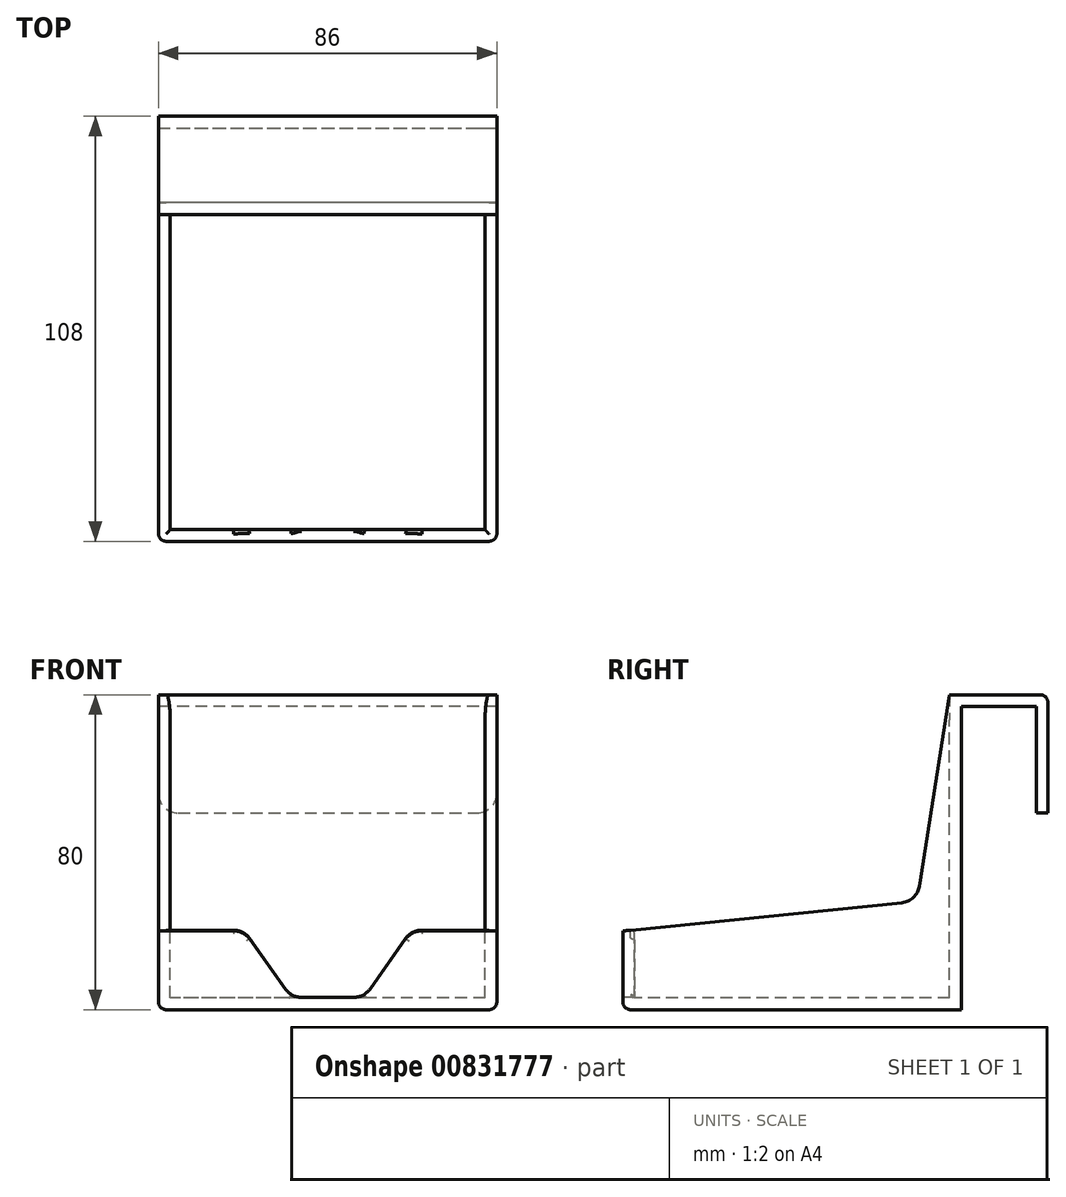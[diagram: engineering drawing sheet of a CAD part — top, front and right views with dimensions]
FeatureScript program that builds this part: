
annotation { "Feature Type Name" : "Feature", "Feature Type Description" : "" }
export const myFeature = defineFeature(function(context is Context, id is Id, definition is map)
    precondition{}
    {
        {
            var Q0;
            Q0=qCreatedBy(makeId("Top.planeOp"),FACE);
            var sketch = newSketch(context, id + "F0", { "sketchPlane" : qUnion([Q0])});
            skLineSegment(sketch, "E0.bottom", {"start": v(43, 43) * mm, "end": v(-43, 43) * mm});
            skLineSegment(sketch, "E0.top", {"start": v(43, -43) * mm, "end": v(-43, -43) * mm});
            skLineSegment(sketch, "E0.left", {"start": v(43, 43) * mm, "end": v(43, -43) * mm});
            skLineSegment(sketch, "E0.right", {"start": v(-43, 43) * mm, "end": v(-43, -43) * mm});
            skPoint(sketch, "E0.middle", {"position": v(0, 0) * mm});
            skLineSegment(sketch, "E1", {"start": v(-43, 43) * mm, "end": v(-43, 62) * mm});
            skLineSegment(sketch, "E2", {"start": v(43, 43) * mm, "end": v(43, 62) * mm});
            skLineSegment(sketch, "E3", {"start": v(-43, 62) * mm, "end": v(43, 62) * mm});
            skLineSegment(sketch, "E4", {"start": v(-43, 62) * mm, "end": v(-43, 64) * mm});
            skLineSegment(sketch, "E5", {"start": v(43, 62) * mm, "end": v(43, 64) * mm});
            skLineSegment(sketch, "E6", {"start": v(43, 64) * mm, "end": v(-43, 64) * mm});
            skSolve(sketch);
        }
        {
            var Q0;
            Q0=makeQuery(id+"F0.imprint","IMPRINT",FACE,{"disambiguationData":[TD([[makeQuery(id+"F0.imprint","IMPRINT",EDGE,{"derivedFrom":sQuery(id+"F0.wireOp",EDGE,"E0.bottom")}),1.0]])]});
            extrude(context, id + "F1", {"entities" : qUnion([Q0]), "depth" : 80 * mm, "offsetDistance" : 25 * mm});
        }
        {
            var Q0;
            Q0=makeQuery(id+"F1.opExtrude","CAP_FACE",FACE,{"disambiguationData":[OSD([sQuery(id+"F0.wireOp",EDGE,"E0.bottom"),sQuery(id+"F0.wireOp",EDGE,"E0.top"),sQuery(id+"F0.wireOp",EDGE,"E0.left"),sQuery(id+"F0.wireOp",EDGE,"E0.right")])],"isStart":false});
            var sketch = newSketch(context, id + "F2", { "sketchPlane" : qUnion([Q0])});
            skLineSegment(sketch, "E7", {"start": v(43, 43) * mm, "end": v(43, 62) * mm});
            skLineSegment(sketch, "E8", {"start": v(-43, 43) * mm, "end": v(-43, 62) * mm});
            skLineSegment(sketch, "E9", {"start": v(-43, 62) * mm, "end": v(43, 62) * mm});
            skLineSegment(sketch, "E10", {"start": v(-43, 62) * mm, "end": v(-43, 65) * mm});
            skLineSegment(sketch, "E11", {"start": v(43, 62) * mm, "end": v(43, 65) * mm});
            skLineSegment(sketch, "E12", {"start": v(-43, 65) * mm, "end": v(43, 65) * mm});
            skSolve(sketch);
        }
        {
            var Q0;
            Q0=makeQuery(id+"F2.imprint","IMPRINT",FACE,{"disambiguationData":[TD([[makeQuery(id+"F2.imprint","IMPRINT",EDGE,{"derivedFrom":sQuery(id+"F2.wireOp",EDGE,"E7")}),1.0]])]});
            extrude(context, id + "F3", {"entities" : qUnion([Q0]), "operationType" : NewBodyOperationType.ADD, "depth" : -3 * mm, "offsetDistance" : 25 * mm});
        }
        {
            var Q0;
            Q0=qSketchRegion(id+"F2",true);
            var Q1;
            Q1=makeQuery(id+"F2.imprint","IMPRINT",FACE,{"disambiguationData":[TD([[makeQuery(id+"F2.imprint","IMPRINT",EDGE,{"derivedFrom":sQuery(id+"F2.wireOp",EDGE,"E9")}),1.0]])]});
            extrude(context, id + "F4", {"entities" : qUnion([Q0, Q1]), "operationType" : NewBodyOperationType.ADD, "depth" : -30 * mm, "offsetDistance" : 25 * mm});
        }
        {
            var Q0;
            Q0=makeQuery(id+"F2.imprint","IMPRINT",FACE,{"disambiguationData":[TD([[makeQuery(id+"F2.imprint","IMPRINT",EDGE,{"derivedFrom":makeQuery(id+"F1.opExtrude","CAP_EDGE",EDGE,{"disambiguationData":[OSD([sQuery(id+"F0.wireOp",EDGE,"E0.bottom")])],"isStart":false})}),1.0]])]});
            var sketch = newSketch(context, id + "F5", { "sketchPlane" : qUnion([Q0])});
            skLineSegment(sketch, "E13.bottom", {"start": v(40, 40) * mm, "end": v(-40, 40) * mm});
            skLineSegment(sketch, "E13.top", {"start": v(40, -40) * mm, "end": v(-40, -40) * mm});
            skLineSegment(sketch, "E13.left", {"start": v(40, 40) * mm, "end": v(40, -40) * mm});
            skLineSegment(sketch, "E13.right", {"start": v(-40, 40) * mm, "end": v(-40, -40) * mm});
            skPoint(sketch, "E13.middle", {"position": v(0, 0) * mm});
            skSolve(sketch);
        }
        {
            var Q0;
            Q0=makeQuery(id+"F5.imprint","IMPRINT",FACE,{"disambiguationData":[TD([[makeQuery(id+"F5.imprint","IMPRINT",EDGE,{"derivedFrom":sQuery(id+"F5.wireOp",EDGE,"E13.bottom")}),1.0]])]});
            extrude(context, id + "F6", {"entities" : qUnion([Q0]), "operationType" : NewBodyOperationType.REMOVE, "oppositeDirection" : true, "depth" : 77 * mm, "offsetDistance" : 25 * mm});
        }
        {
            var Q0;
            Q0=makeQuery(id+"F4.boolean.opBoolean","MERGE",FACE,{"derivedFrom":[makeQuery(id+"F3.boolean.opBoolean","MERGE",FACE,{"derivedFrom":[makeQuery(id+"F1.opExtrude","SWEPT_FACE",FACE,{"disambiguationData":[OSD([sQuery(id+"F0.wireOp",EDGE,"E0.left")])]}),makeQuery(id+"F3.opExtrude","SWEPT_FACE",FACE,{"disambiguationData":[OSD([sQuery(id+"F2.wireOp",EDGE,"E7")])]})]}),makeQuery(id+"F4.opExtrude","SWEPT_FACE",FACE,{"disambiguationData":[OSD([sQuery(id+"F2.wireOp",EDGE,"E11")])]})]});
            var sketch = newSketch(context, id + "F7", { "sketchPlane" : qUnion([Q0])});
            skLineSegment(sketch, "E14", {"start": v(-43, 80) * mm, "end": v(-43, 20) * mm});
            skLineSegment(sketch, "E15", {"start": v(-43, 20) * mm, "end": v(40, 80) * mm});
            skLineSegment(sketch, "E16", {"start": v(40, 80) * mm, "end": v(-43, 80) * mm});
            skSolve(sketch);
        }
        {
            var Q0;
            Q0=makeQuery(id+"F7.imprint","IMPRINT",FACE,{"disambiguationData":[TD([[makeQuery(id+"F7.imprint","IMPRINT",EDGE,{"derivedFrom":sQuery(id+"F7.wireOp",EDGE,"E14")}),1.0]])]});
            extrude(context, id + "F8", {"entities" : qUnion([Q0]), "operationType" : NewBodyOperationType.REMOVE, "oppositeDirection" : true, "depth" : 100 * mm, "offsetDistance" : 25 * mm});
        }
        {
            var Q0;
            Q0=makeQuery(id+"F4.opExtrude","CAP_EDGE",EDGE,{"disambiguationData":[OSD([sQuery(id+"F2.wireOp",EDGE,"E11")])],"isStart":false});
            var Q1;
            Q1=makeQuery(id+"F4.opExtrude","CAP_EDGE",EDGE,{"disambiguationData":[OSD([sQuery(id+"F2.wireOp",EDGE,"E10")])],"isStart":false});
            fillet(context, id + "F9", {"entities" : qUnion([Q0, Q1]), "radius" : 5 * mm, "tangentPropagation" : true, "allowEdgeOverflow" : false});
        }
        {
            var Q0;
            Q0=makeQuery(id+"F4.opExtrude","CAP_EDGE",EDGE,{"disambiguationData":[OSD([sQuery(id+"F2.wireOp",EDGE,"E12")])],"isStart":true});
            fillet(context, id + "F10", {"entities" : qUnion([Q0]), "radius" : 2 * mm, "tangentPropagation" : true, "allowEdgeOverflow" : false});
        }
        {
            var Q0;
            Q0=makeQuery(id+"F1.opExtrude","SWEPT_FACE",FACE,{"disambiguationData":[OSD([sQuery(id+"F0.wireOp",EDGE,"E0.top")])]});
            var sketch = newSketch(context, id + "F11", { "sketchPlane" : qUnion([Q0])});
            skLineSegment(sketch, "E17", {"start": v(0, 3.11) * mm, "end": v(9.22, 3.11) * mm});
            skLineSegment(sketch, "E18", {"start": v(9.22, 3.11) * mm, "end": v(23.02, 22.56) * mm});
            skLineSegment(sketch, "E19", {"start": v(23.02, 22.56) * mm, "end": v(0, 22.56) * mm});
            skLineSegment(sketch, "E20", {"start": v(0, 22.56) * mm, "end": v(-23.02, 22.56) * mm});
            skLineSegment(sketch, "E21", {"start": v(-23.02, 22.56) * mm, "end": v(-9.22, 3.11) * mm});
            skLineSegment(sketch, "E22", {"start": v(-9.22, 3.11) * mm, "end": v(0, 3.11) * mm});
            skSolve(sketch);
        }
        {
            var Q0;
            Q0 = qSketchRegion(id + "F11", true);
            var Q1;
            {var subQ4=sQuery(id+"F11.wireOp",EDGE,"E19");Q1=makeQuery(id+"F11.imprint","IMPRINT",FACE,{"disambiguationData":[TD([[makeQuery(id+"F11.imprint","IMPRINT",EDGE,{"derivedFrom":subQ4}),1.0]])]});}
            var Q2;
            {var subQ5=sQuery(id+"F11.wireOp",EDGE,"E17");Q2=makeQuery(id+"F11.imprint","IMPRINT",FACE,{"disambiguationData":[TD([[makeQuery(id+"F11.imprint","IMPRINT",EDGE,{"derivedFrom":subQ5}),1.0]])]});}
            extrude(context, id + "F12", {"entities" : qUnion([Q0, Q1, Q2]), "operationType" : NewBodyOperationType.REMOVE, "oppositeDirection" : true, "depth" : 10 * mm, "offsetDistance" : 25 * mm});
        }
        {
            var Q0;
            Q0=makeQuery(id+"F4.boolean.opBoolean","MERGE",FACE,{"derivedFrom":[makeQuery(id+"F3.boolean.opBoolean","MERGE",FACE,{"derivedFrom":[makeQuery(id+"F1.opExtrude","SWEPT_FACE",FACE,{"disambiguationData":[OSD([sQuery(id+"F0.wireOp",EDGE,"E0.left")])]}),makeQuery(id+"F3.opExtrude","SWEPT_FACE",FACE,{"disambiguationData":[OSD([sQuery(id+"F2.wireOp",EDGE,"E7")])]})]}),makeQuery(id+"F4.opExtrude","SWEPT_FACE",FACE,{"disambiguationData":[OSD([sQuery(id+"F2.wireOp",EDGE,"E11")])]})]});
            var sketch = newSketch(context, id + "F13", { "sketchPlane" : qUnion([Q0])});
            skLineSegment(sketch, "E23", {"start": v(40, 80) * mm, "end": v(31.74, 27.57) * mm});
            skLineSegment(sketch, "E24", {"start": v(31.74, 27.57) * mm, "end": v(-43, 20) * mm});
            skLineSegment(sketch, "E25", {"start": v(-43, 20) * mm, "end": v(40, 80) * mm});
            skSolve(sketch);
        }
        {
            var Q0;
            Q0=makeQuery(id+"F13.imprint","IMPRINT",FACE,{"disambiguationData":[TD([[makeQuery(id+"F13.imprint","IMPRINT",EDGE,{"derivedFrom":sQuery(id+"F13.wireOp",EDGE,"E23")}),-1.0]])]});
            extrude(context, id + "F14", {"entities" : qUnion([Q0]), "operationType" : NewBodyOperationType.REMOVE, "oppositeDirection" : true, "depth" : 100 * mm, "offsetDistance" : 25 * mm});
        }
        {
            var Q0;
            Q0=makeQuery(id+"F14.boolean.opBoolean","INTERSECT",EDGE,{"derivedFrom":[makeQuery(id+"F12.boolean.opBoolean","COPY",FACE,{"derivedFrom":makeQuery(id+"F12.opExtrude","SWEPT_FACE",FACE,{"disambiguationData":[OSD([sQuery(id+"F11.wireOp",EDGE,"E18")])]})}),makeQuery(id+"F14.opExtrude","SWEPT_FACE",FACE,{"disambiguationData":[OSD([sQuery(id+"F13.wireOp",EDGE,"E24")])]})]});
            var Q1;
            Q1=makeQuery(id+"F14.boolean.opBoolean","INTERSECT",EDGE,{"derivedFrom":[makeQuery(id+"F12.boolean.opBoolean","COPY",FACE,{"derivedFrom":makeQuery(id+"F12.opExtrude","SWEPT_FACE",FACE,{"disambiguationData":[OSD([sQuery(id+"F11.wireOp",EDGE,"E21")])]})}),makeQuery(id+"F14.opExtrude","SWEPT_FACE",FACE,{"disambiguationData":[OSD([sQuery(id+"F13.wireOp",EDGE,"E24")])]})]});
            var Q2;
            Q2=makeQuery(id+"F12.boolean.opBoolean","COPY",EDGE,{"derivedFrom":makeQuery(id+"F12.opExtrude","SWEPT_EDGE",EDGE,{"disambiguationData":[OSD([sQuery(id+"F11.wireOp",EDGE,"E21"),sQuery(id+"F11.wireOp",EDGE,"E22")])]})});
            var Q3;
            Q3=makeQuery(id+"F12.boolean.opBoolean","COPY",EDGE,{"derivedFrom":makeQuery(id+"F12.opExtrude","SWEPT_EDGE",EDGE,{"disambiguationData":[OSD([sQuery(id+"F11.wireOp",EDGE,"E17"),sQuery(id+"F11.wireOp",EDGE,"E18")])]})});
            fillet(context, id + "F15", {"entities" : qUnion([Q0, Q1, Q2, Q3]), "radius" : 5 * mm, "tangentPropagation" : true, "allowEdgeOverflow" : false});
        }
        {
            var Q0;
            {var subQ0=sQuery(id+"F13.wireOp",EDGE,"E23");var subQ1=sQuery(id+"F13.wireOp",EDGE,"E24");Q0=makeQuery(id+"F14.boolean.opBoolean","COPY",EDGE,{"disambiguationData":[TD([makeQuery(id+"F1.opExtrude","SWEPT_FACE",FACE,{"disambiguationData":[OSD([sQuery(id+"F0.wireOp",EDGE,"E0.right")])]})])],"derivedFrom":makeQuery(id+"F14.opExtrude","SWEPT_EDGE",EDGE,{"disambiguationData":[OSD([subQ0,subQ1])]})});}
            var Q1;
            {var subQ0=sQuery(id+"F13.wireOp",EDGE,"E23");var subQ1=sQuery(id+"F13.wireOp",EDGE,"E24");Q1=makeQuery(id+"F14.boolean.opBoolean","COPY",EDGE,{"disambiguationData":[TD([makeQuery(id+"F1.opExtrude","SWEPT_FACE",FACE,{"disambiguationData":[OSD([sQuery(id+"F0.wireOp",EDGE,"E0.left")])]})])],"derivedFrom":makeQuery(id+"F14.opExtrude","SWEPT_EDGE",EDGE,{"disambiguationData":[OSD([subQ0,subQ1])]})});}
            fillet(context, id + "F16", {"entities" : qUnion([Q0, Q1]), "radius" : 5 * mm, "tangentPropagation" : true, "allowEdgeOverflow" : false});
        }
        {
            var Q0;
            Q0=makeQuery(id+"F12.boolean.opBoolean","INTERSECT",EDGE,{"derivedFrom":[makeQuery(id+"F6.boolean.opBoolean","COPY",FACE,{"derivedFrom":makeQuery(id+"F6.opExtrude","SWEPT_FACE",FACE,{"disambiguationData":[OSD([sQuery(id+"F5.wireOp",EDGE,"E13.top")])]})}),makeQuery(id+"F12.opExtrude","SWEPT_FACE",FACE,{"disambiguationData":[OSD([sQuery(id+"F11.wireOp",EDGE,"E21")])]})]});
            var Q1;
            Q1=makeQuery(id+"F14.boolean.opBoolean","INTERSECT",EDGE,{"disambiguationData":[OD(1.0)],"derivedFrom":[makeQuery(id+"F6.boolean.opBoolean","COPY",FACE,{"derivedFrom":makeQuery(id+"F6.opExtrude","SWEPT_FACE",FACE,{"disambiguationData":[OSD([sQuery(id+"F5.wireOp",EDGE,"E13.top")])]})}),makeQuery(id+"F14.opExtrude","SWEPT_FACE",FACE,{"disambiguationData":[OSD([sQuery(id+"F13.wireOp",EDGE,"E24")])]})]});
            var Q2;
            Q2=makeQuery(id+"F14.boolean.opBoolean","INTERSECT",EDGE,{"derivedFrom":[makeQuery(id+"F6.boolean.opBoolean","COPY",FACE,{"derivedFrom":makeQuery(id+"F6.opExtrude","SWEPT_FACE",FACE,{"disambiguationData":[OSD([sQuery(id+"F5.wireOp",EDGE,"E13.left")])]})}),makeQuery(id+"F14.opExtrude","SWEPT_FACE",FACE,{"disambiguationData":[OSD([sQuery(id+"F13.wireOp",EDGE,"E24")])]})]});
            var Q3;
            Q3=makeQuery(id+"F14.boolean.opBoolean","INTERSECT",EDGE,{"derivedFrom":[makeQuery(id+"F6.boolean.opBoolean","COPY",FACE,{"derivedFrom":makeQuery(id+"F6.opExtrude","SWEPT_FACE",FACE,{"disambiguationData":[OSD([sQuery(id+"F5.wireOp",EDGE,"E13.right")])]})}),makeQuery(id+"F14.opExtrude","SWEPT_FACE",FACE,{"disambiguationData":[OSD([sQuery(id+"F13.wireOp",EDGE,"E24")])]})]});
            var Q4;
            Q4=makeQuery(id+"F14.boolean.opBoolean","INTERSECT",EDGE,{"derivedFrom":[makeQuery(id+"F6.boolean.opBoolean","COPY",FACE,{"derivedFrom":makeQuery(id+"F6.opExtrude","SWEPT_FACE",FACE,{"disambiguationData":[OSD([sQuery(id+"F5.wireOp",EDGE,"E13.left")])]})}),makeQuery(id+"F14.opExtrude","SWEPT_FACE",FACE,{"disambiguationData":[OSD([sQuery(id+"F13.wireOp",EDGE,"E23")])]})]});
            var Q5;
            Q5=makeQuery(id+"F14.boolean.opBoolean","INTERSECT",EDGE,{"disambiguationData":[OD(0.0)],"derivedFrom":[makeQuery(id+"F6.boolean.opBoolean","COPY",FACE,{"derivedFrom":makeQuery(id+"F6.opExtrude","SWEPT_FACE",FACE,{"disambiguationData":[OSD([sQuery(id+"F5.wireOp",EDGE,"E13.top")])]})}),makeQuery(id+"F14.opExtrude","SWEPT_FACE",FACE,{"disambiguationData":[OSD([sQuery(id+"F13.wireOp",EDGE,"E24")])]})]});
            var Q6;
            Q6=makeQuery(id+"F14.boolean.opBoolean","INTERSECT",EDGE,{"derivedFrom":[makeQuery(id+"F6.boolean.opBoolean","COPY",FACE,{"derivedFrom":makeQuery(id+"F6.opExtrude","SWEPT_FACE",FACE,{"disambiguationData":[OSD([sQuery(id+"F5.wireOp",EDGE,"E13.right")])]})}),makeQuery(id+"F14.opExtrude","SWEPT_FACE",FACE,{"disambiguationData":[OSD([sQuery(id+"F13.wireOp",EDGE,"E23")])]})]});
            fillet(context, id + "F17", {"entities" : qUnion([Q0, Q1, Q2, Q3, Q4, Q5, Q6]), "radius" : 1 * mm, "tangentPropagation" : true, "allowEdgeOverflow" : false});
        }
        {
            var Q0;
            Q0=makeQuery(id+"F1.opExtrude","SWEPT_EDGE",EDGE,{"disambiguationData":[OSD([sQuery(id+"F0.wireOp",EDGE,"E0.top"),sQuery(id+"F0.wireOp",EDGE,"E0.right")])]});
            var Q1;
            Q1=makeQuery(id+"F1.opExtrude","SWEPT_EDGE",EDGE,{"disambiguationData":[OSD([sQuery(id+"F0.wireOp",EDGE,"E0.top"),sQuery(id+"F0.wireOp",EDGE,"E0.left")])]});
            var Q2;
            Q2=makeQuery(id+"F1.opExtrude","CAP_EDGE",EDGE,{"disambiguationData":[OSD([sQuery(id+"F0.wireOp",EDGE,"E0.right")])],"isStart":true});
            var Q3;
            Q3=makeQuery(id+"F1.opExtrude","CAP_EDGE",EDGE,{"disambiguationData":[OSD([sQuery(id+"F0.wireOp",EDGE,"E0.top")])],"isStart":true});
            var Q4;
            Q4=makeQuery(id+"F1.opExtrude","CAP_EDGE",EDGE,{"disambiguationData":[OSD([sQuery(id+"F0.wireOp",EDGE,"E0.left")])],"isStart":true});
            fillet(context, id + "F18", {"entities" : qUnion([Q0, Q1, Q2, Q3, Q4]), "radius" : 2 * mm, "tangentPropagation" : true, "allowEdgeOverflow" : false});
        }
    });
